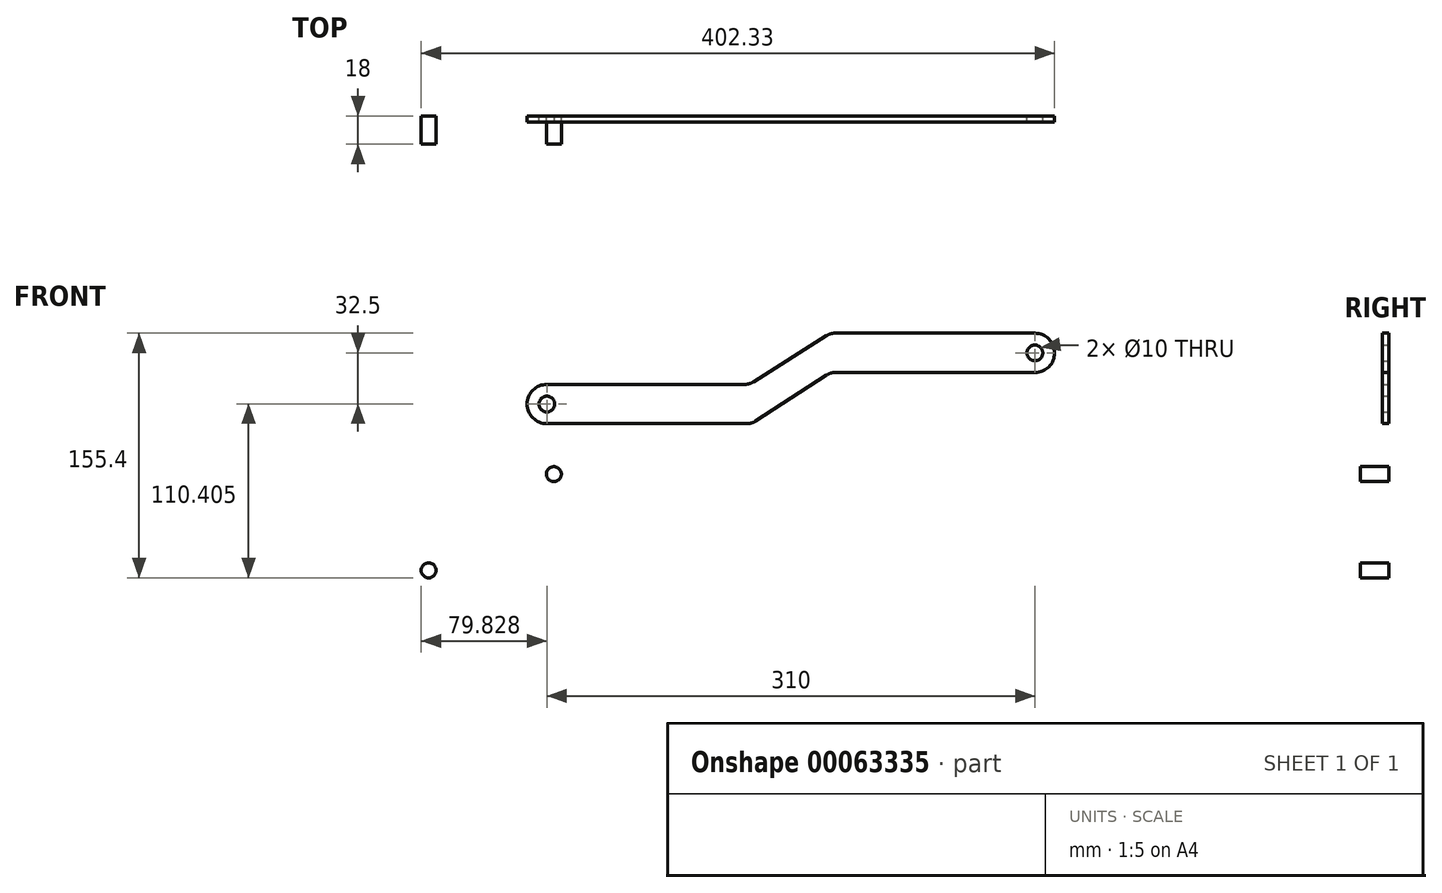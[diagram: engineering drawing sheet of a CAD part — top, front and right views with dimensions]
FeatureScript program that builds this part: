
annotation { "Feature Type Name" : "Feature", "Feature Type Description" : "" }
export const myFeature = defineFeature(function(context is Context, id is Id, definition is map)
    precondition{}
    {
        {
            var Q0;
            Q0=qCreatedBy(makeId("Front.planeOp"),FACE);
            var sketch = newSketch(context, id + "F0", { "sketchPlane" : qUnion([Q0])});
            skLineSegment(sketch, "E0.right", {"start": v(132.6, 67.34) * mm, "end": v(132.6, 67.34) * mm});
            skPoint(sketch, "E1.visualSharp", {"position": v(132.6, 54.84) * mm});
            skPoint(sketch, "E2.visualSharp", {"position": v(132.6, 79.84) * mm});
            skPoint(sketch, "E3.visualSharp", {"position": v(-9.9, 54.84) * mm});
            skPoint(sketch, "E4.visualSharp", {"position": v(-9.9, 79.84) * mm});
            skPoint(sketch, "E5.visualSharp", {"position": v(-59.9, 22.34) * mm});
            skLineSegment(sketch, "E6.bottom", {"start": v(-62.86, 22.34) * mm, "end": v(-189.9, 22.34) * mm});
            skLineSegment(sketch, "E6.top", {"start": v(-64.1, 47.34) * mm, "end": v(-189.9, 47.34) * mm});
            skLineSegment(sketch, "E0.bottom", {"start": v(-7, 79.84) * mm, "end": v(120.1, 79.84) * mm});
            skLineSegment(sketch, "E0.top", {"start": v(-6.93, 54.84) * mm, "end": v(120.1, 54.84) * mm});
            skLineSegment(sketch, "E7", {"start": v(-58.75, 48.9) * mm, "end": v(-12.34, 78.3) * mm});
            skLineSegment(sketch, "E8", {"start": v(-12.38, 53.23) * mm, "end": v(-57.4, 23.96) * mm});
            skPoint(sketch, "E9.rect.middle", {"position": v(-34.9, 51.1) * mm});
            skPoint(sketch, "E10.visualSharp", {"position": v(-61.2, 47.34) * mm});
            skPoint(sketch, "E11.orphan", {"position": v(-64.47, 75.96) * mm});
            skPoint(sketch, "E12.orphan", {"position": v(-5.31, 26.23) * mm});
            skPoint(sketch, "E13.visualSharp", {"position": v(-197.4, 22.34) * mm});
            skPoint(sketch, "E14.visualSharp", {"position": v(-197.4, 47.34) * mm});
            skArc(sketch, "E1.filletArc", {"start": v(120.1, 54.84) * mm, "mid": v(128.95, 58.5) * mm, "end": v(132.6, 67.34) * mm});
            skArc(sketch, "E2.filletArc", {"start": v(132.6, 67.34) * mm, "mid": v(128.95, 76.18) * mm, "end": v(120.1, 79.84) * mm});
            skLineSegment(sketch, "E15.bottom", {"start": v(-189.9, 47.34) * mm, "end": v(-172.62, 47.34) * mm});
            skArc(sketch, "E10.filletArc", {"start": v(-64.1, 47.34) * mm, "mid": v(-61.31, 47.74) * mm, "end": v(-58.75, 48.9) * mm});
            skArc(sketch, "E4.filletArc", {"start": v(-7, 79.84) * mm, "mid": v(-9.78, 79.45) * mm, "end": v(-12.34, 78.3) * mm});
            skArc(sketch, "E5.filletArc", {"start": v(-62.86, 22.34) * mm, "mid": v(-60.01, 22.76) * mm, "end": v(-57.4, 23.96) * mm});
            skArc(sketch, "E3.filletArc", {"start": v(-6.93, 54.84) * mm, "mid": v(-9.77, 54.43) * mm, "end": v(-12.38, 53.23) * mm});
            skPoint(sketch, "E14.filletArc.center.orphan", {"position": v(-187.4, 37.34) * mm});
            skArc(sketch, "E16", {"start": v(-189.9, 47.34) * mm, "mid": v(-202.4, 34.84) * mm, "end": v(-189.9, 22.34) * mm});
            skPoint(sketch, "E17.center.orphan", {"position": v(120.1, 69.84) * mm});
            skCircle(sketch, "E18", {"center": v(-189.9, 34.84) * mm, "radius": 5 * mm});
            skCircle(sketch, "E19", {"center": v(120.1, 67.34) * mm, "radius": 5 * mm});
            skCircle(sketch, "E20", {"center": v(-185.42, -9.67) * mm, "radius": 4.75 * mm});
            skCircle(sketch, "E21", {"center": v(-264.97, -70.81) * mm, "radius": 4.75 * mm});
            skSolve(sketch);
        }
        {
            var Q0;
            Q0 = qSketchRegion(id + "F0", true);
            extrude(context, id + "F1", {"entities" : qUnion([Q0]), "depth" : 4 * mm});
        }
        {
            var Q0;
            Q0=makeQuery(id+"F1.opExtrude","CAP_FACE",FACE,{"disambiguationData":[OSD([sQuery(id+"F0.wireOp",EDGE,"E20")])],"isStart":false});
            extrude(context, id + "F2", {"entities" : qUnion([Q0]), "operationType" : NewBodyOperationType.ADD, "depth" : 14 * mm});
        }
        {
            var Q0;
            Q0=makeQuery(id+"F1.opExtrude","CAP_FACE",FACE,{"disambiguationData":[OSD([sQuery(id+"F0.wireOp",EDGE,"E21")])],"isStart":false});
            extrude(context, id + "F3", {"entities" : qUnion([Q0]), "operationType" : NewBodyOperationType.ADD, "depth" : 14 * mm});
        }
    });
